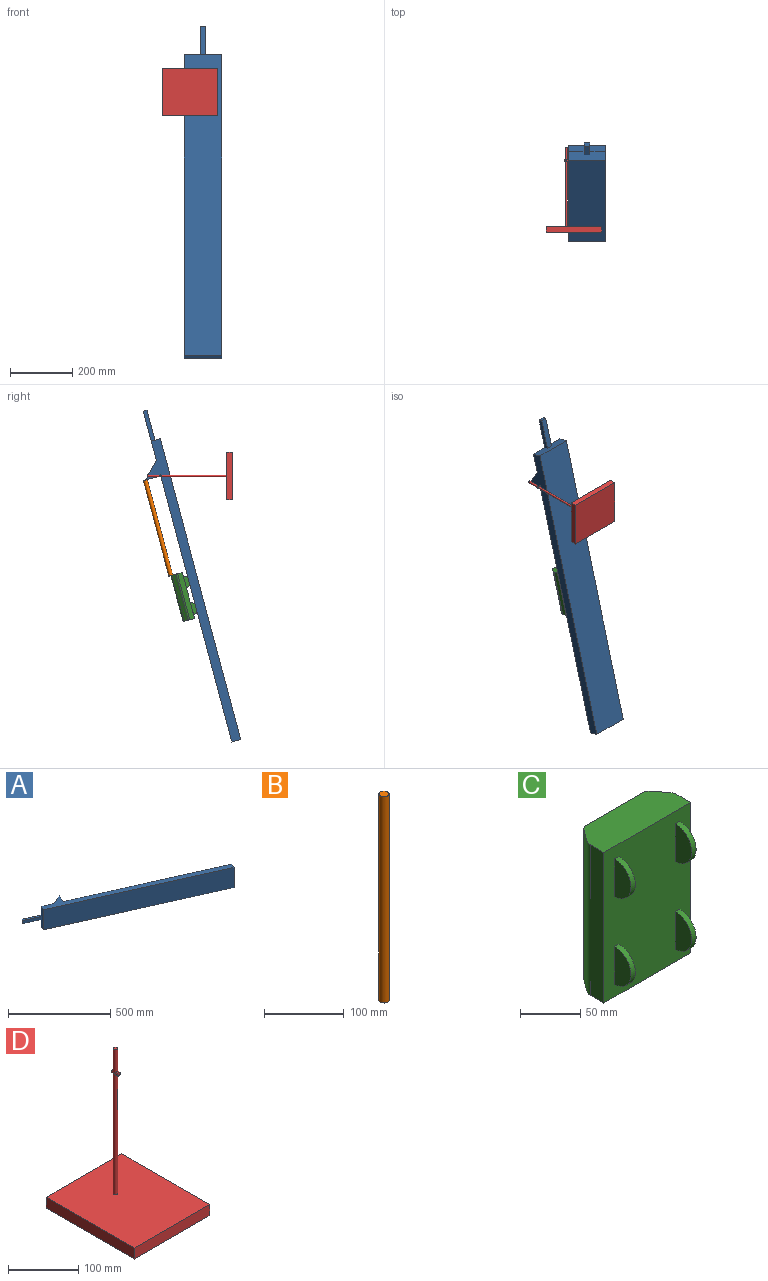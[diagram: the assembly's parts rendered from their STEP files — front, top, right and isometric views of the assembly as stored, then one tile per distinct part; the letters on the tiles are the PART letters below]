
ASSEMBLY  parts=4 mates=3
PART A: 13 faces, bbox 1010.2x474.6x120 mm
  f0: plane 807.76x359.39mm, normal (0.41,0.91,0), area 106092mm2, adj f5,f7,f8,f11
  f1: plane 91.37x40.65mm, normal (-0.41,-0.91,0), area 1840mm2, adj f2,f3,f9,f10
  f2: plane 18.4x11.6mm, normal (-0.91,0.41,0), area 233.7mm2, adj f1,f6,f9,f10
  f3: plane 120x27.41mm, normal (-0.91,0.41,0), area 3366.3mm2, adj f1,f4,f6,f7,f8,f9,f10
  f4: plane 913.65x406.5mm, normal (-0.41,-0.91,0), area 120000mm2, adj f3,f5,f7,f8
  f5: plane 120x27.41mm, normal (0.91,-0.41,0), area 3600mm2, adj f0,f4,f7,f8
  f6: plane 150.84x120mm, normal (0.41,0.91,0), area 9652mm2, adj f2,f3,f7,f8,f9,f10,f12
  f7: plane 925.85x433.91mm, normal (0,0,1), area 31290.3mm2, adj f0,f3,f4,f5,f6,f11,f12
  f8: plane 925.85x433.91mm, normal (0,0,-1), area 31290.3mm2, adj f0,f3,f4,f5,f6,f11,f12
  f9: plane 96.53x52.25mm, normal (0,0,1), area 1270mm2, adj f1,f2,f3,f6
  f10: plane 96.53x52.25mm, normal (0,0,-1), area 1270mm2, adj f1,f2,f3,f6
  f11: plane 120x46.41mm, normal (0.91,-0.41,0), area 6096mm2, adj f0,f7,f8,f12
  f12: plane 120x67.06mm, normal (-0.36,0.93,0), area 8621mm2, adj f6,f7,f8,f11
PART B: 3 faces, bbox 12.7x12.7x317.5 mm
  f0: cylinder r=6.35mm len=317.5mm, axis (0,0,-1), area 12667.7mm2, adj f1,f2
  f1: plane 12.7x12.7mm, normal (0,0,1), area 126.7mm2, adj f0
  f2: plane 12.7x12.7mm, normal (0,0,-1), area 126.7mm2, adj f0
PART C: 24 faces, bbox 101.6x57.2x152.4 mm
  f0: plane 152.4x101.6mm, normal (0,-1,0), area 14709.6mm2, adj f1,f5,f6,f7,f12,f13,f14,f15
  f1: plane 152.4x16.14mm, normal (1,0,0), area 2459.7mm2, adj f0,f6,f7,f10
  f2: plane 152.4x13.07mm, normal (0.81,0.59,0), area 2470.1mm2, adj f6,f7,f10,f11
  f3: plane 152.4x64.65mm, normal (0,1,0), area 9852.7mm2, adj f6,f7,f8,f11
  f4: plane 152.4x13.07mm, normal (-0.81,0.59,0), area 2470.1mm2, adj f6,f7,f8,f9
  f5: plane 152.4x16.14mm, normal (-1,0,0), area 2459.7mm2, adj f0,f6,f7,f9
  f6: plane 101.6x38.1mm, normal (0,0,1), area 3597.1mm2, adj f0,f1,f2,f3,f4,f5,f8,f9
  f7: plane 101.6x38.1mm, normal (0,0,-1), area 3597.1mm2, adj f0,f1,f2,f3,f4,f5,f8,f9
  f8: cylinder r=8.89mm len=152.4mm, axis (0,0,-1), area 1270.9mm2, adj f3,f4,f6,f7
  f9: cylinder r=8.89mm len=152.4mm, axis (0,0,-1), area 857.3mm2, adj f4,f5,f6,f7
  f10: cylinder r=8.89mm len=152.4mm, axis (0,0,-1), area 857.3mm2, adj f1,f2,f6,f7
  f11: cylinder r=8.89mm len=152.4mm, axis (0,0,-1), area 1270.9mm2, adj f2,f3,f6,f7
  f12: cylinder r=19.05mm len=38.1mm, axis (-1,0,0), area 304mm2, adj f0,f13,f14
  f13: plane 38.1x19.05mm, normal (-1,0,0), area 570mm2, adj f0,f12
  f14: plane 38.1x19.05mm, normal (1,0,0), area 570mm2, adj f0,f12
  f15: cylinder r=19.05mm len=38.1mm, axis (-1,0,0), area 304mm2, adj f0,f16,f17
  f16: plane 38.1x19.05mm, normal (-1,0,0), area 570mm2, adj f0,f15
  f17: plane 38.1x19.05mm, normal (1,0,0), area 570mm2, adj f0,f15
  f18: plane 38.1x19.05mm, normal (-1,0,0), area 570mm2, adj f0,f19
  f19: cylinder r=19.05mm len=38.1mm, axis (-1,0,0), area 304mm2, adj f0,f18,f20
  f20: plane 38.1x19.05mm, normal (1,0,0), area 570mm2, adj f0,f19
  f21: plane 38.1x19.05mm, normal (-1,0,0), area 570mm2, adj f0,f22
  f22: cylinder r=19.05mm len=38.1mm, axis (-1,0,0), area 304mm2, adj f0,f21,f23
  f23: plane 38.1x19.05mm, normal (1,0,0), area 570mm2, adj f0,f22
PART D: 11 faces, bbox 152.4x177.8x273.1 mm
  f0: cylinder r=3.17mm len=11.18mm, axis (0,1,0), area 143.1mm2, adj f1,f9,f10
  f1: cylinder r=3.17mm len=254mm, axis (0,0,-1), area 4987.2mm2, adj f0,f5,f8
  f2: plane 177.8x19.05mm, normal (-1,0,0), area 3387.1mm2, adj f3,f5,f6,f7
  f3: plane 177.8x152.4mm, normal (0,0,-1), area 27096.7mm2, adj f2,f4,f6,f7
  f4: plane 177.8x19.05mm, normal (1,0,0), area 3387.1mm2, adj f3,f5,f6,f7
  f5: plane 177.8x152.4mm, normal (0,0,1), area 27065.1mm2, adj f1,f2,f4,f6,f7
  f6: plane 152.4x19.05mm, normal (0,-1,0), area 2903.2mm2, adj f2,f3,f4,f5
  f7: plane 152.4x19.05mm, normal (0,1,0), area 2903.2mm2, adj f2,f3,f4,f5
  f8: plane 6.35x6.35mm, normal (0,0,1), area 31.7mm2, adj f1
  f9: plane 6.35x6.35mm, normal (0,-1,0), area 31.7mm2, adj f0
  f10: plane 6.35x6.35mm, normal (0,1,0), area 31.7mm2, adj f0
PLACE A rot(axis=(0.08,0.99,0.08),90.4deg) t=(-107.95,-105.43,-409.31)mm
PLACE B rot(axis=(1,0,0),165deg) t=(-47.95,270.43,-13.53)mm
PLACE C rot(axis=(-1,0,0),15deg) t=(-47.95,112.21,-457.63)mm
PLACE D rot(axis=(-0.58,0.58,0.58),120deg) t=(-177.8,-9.53,76.2)mm
MATE fastened B.f0 <-> A.f11  axis (0,0.26,0.97) through (-47.95,270.43,-13.53)mm
MATE fastened C.f6 <-> B.f0  axis (0,0.26,0.97) through (-47.95,188.4,-320.25)mm
MATE revolute D.f0 <-> A.f8  axis (1,0,0) through (-107.95,221.36,-0.4)mm
